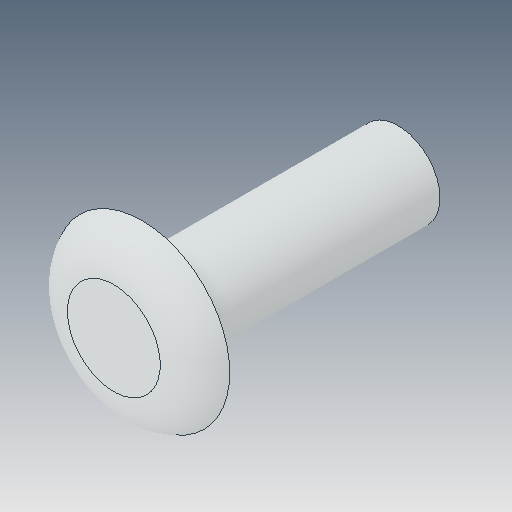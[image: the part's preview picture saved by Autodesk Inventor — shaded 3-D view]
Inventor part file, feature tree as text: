
AUTODESK INVENTOR PART (.ipt)
format: ipt  version: 2023.5 (Build 275446000, 446)  size: 108,032 bytes
history: native  units: in
note: dims shown in document units (in); Inventor stores cm internally (conversion verified against a paired STEP export)
features: fillet x1
ambient origin geometry x8: Origin, YZ Plane, XZ Plane, XY Plane, X Axis, Y Axis, Z Axis, Center Point
bodies: Solid1 (feature_tree)
feature tree (1):
  fillet  "Fillet1"  [1 undecoded]
note: 1 required parameter value undecoded (feature->parameter linkage not recoverable at this tier; creation-order binding heuristic only, values carry confidence <= 0.55)
